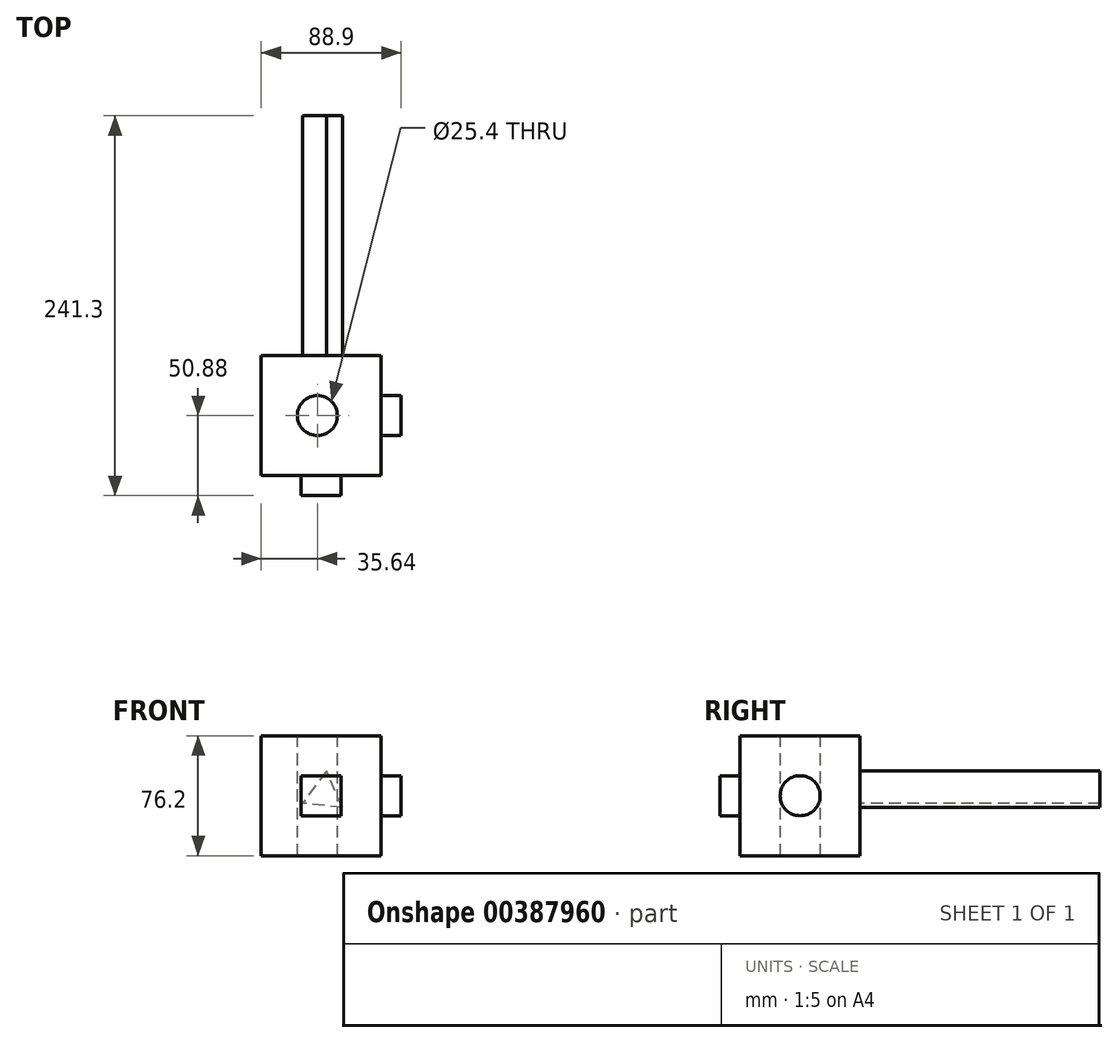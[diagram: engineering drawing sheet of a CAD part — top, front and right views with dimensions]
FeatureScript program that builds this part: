
annotation { "Feature Type Name" : "Feature", "Feature Type Description" : "" }
export const myFeature = defineFeature(function(context is Context, id is Id, definition is map)
    precondition{}
    {
        {
            var Q0;
            Q0=qCreatedBy(makeId("Front.planeOp"),FACE);
            var sketch = newSketch(context, id + "F0", { "sketchPlane" : qUnion([Q0])});
            skLineSegment(sketch, "E0.bottom", {"start": v(-35.64, -57.17) * mm, "end": v(40.56, -57.17) * mm});
            skLineSegment(sketch, "E0.top", {"start": v(-35.64, 19.03) * mm, "end": v(40.56, 19.03) * mm});
            skLineSegment(sketch, "E0.left", {"start": v(-35.64, -57.17) * mm, "end": v(-35.64, 19.03) * mm});
            skLineSegment(sketch, "E0.right", {"start": v(40.56, -57.17) * mm, "end": v(40.56, 19.03) * mm});
            skSolve(sketch);
        }
        {
            var Q0;
            Q0=makeQuery(id+"F0.imprint","IMPRINT",FACE,{"disambiguationData":[TD([[makeQuery(id+"F0.imprint","IMPRINT",EDGE,{"derivedFrom":sQuery(id+"F0.wireOp",EDGE,"E0.bottom")}),1.0]])]});
            extrude(context, id + "F1", {"entities" : qUnion([Q0]), "depth" : 76.2 * mm});
        }
        {
            var Q0;
            Q0=makeQuery(id+"F1.opExtrude","SWEPT_FACE",FACE,{"disambiguationData":[OSD([sQuery(id+"F0.wireOp",EDGE,"E0.top")])]});
            var sketch = newSketch(context, id + "F2", { "sketchPlane" : qUnion([Q0])});
            skPoint(sketch, "E1", {"position": v(0, -38.02) * mm});
            skSolve(sketch);
        }
        {
            var Q0;
            Q0=sQuery(id+"F2.wireOp",VERTEX,"E1");
            var Q1;
            Q1=makeQuery(id+"F1.opExtrude","SWEPT_BODY",BODY,{"disambiguationData":[OSD([sQuery(id+"F0.wireOp",EDGE,"E0.bottom"),sQuery(id+"F0.wireOp",EDGE,"E0.top"),sQuery(id+"F0.wireOp",EDGE,"E0.left"),sQuery(id+"F0.wireOp",EDGE,"E0.right")])]});
            hole(context, id + "F3", {"style" : HoleStyle.SIMPLE, "endStyle" : HoleEndStyle.THROUGH, "holeDiameter" : 25.4 * mm, "isTappedThrough" : true, "tappedDepth" : 12.7 * mm, "tapClearance" : 3, "locations" : qUnion([Q0]), "scope" : qUnion([Q1])});
        }
        {
            var Q0;
            Q0=makeQuery(id+"F1.opExtrude","CAP_FACE",FACE,{"disambiguationData":[OSD([sQuery(id+"F0.wireOp",EDGE,"E0.bottom"),sQuery(id+"F0.wireOp",EDGE,"E0.top"),sQuery(id+"F0.wireOp",EDGE,"E0.left"),sQuery(id+"F0.wireOp",EDGE,"E0.right")])],"isStart":false});
            var sketch = newSketch(context, id + "F4", { "sketchPlane" : qUnion([Q0])});
            skLineSegment(sketch, "E2.bottom", {"start": v(-10.24, -31.77) * mm, "end": v(15.16, -31.77) * mm});
            skLineSegment(sketch, "E2.top", {"start": v(-10.24, -6.37) * mm, "end": v(15.16, -6.37) * mm});
            skLineSegment(sketch, "E2.left", {"start": v(-10.24, -31.77) * mm, "end": v(-10.24, -6.37) * mm});
            skLineSegment(sketch, "E2.right", {"start": v(15.16, -31.77) * mm, "end": v(15.16, -6.37) * mm});
            skSolve(sketch);
        }
        {
            var Q0;
            Q0=makeQuery(id+"F4.imprint","IMPRINT",FACE,{"disambiguationData":[TD([[makeQuery(id+"F4.imprint","IMPRINT",EDGE,{"derivedFrom":sQuery(id+"F4.wireOp",EDGE,"E2.bottom")}),1.0]])]});
            extrude(context, id + "F5", {"entities" : qUnion([Q0]), "operationType" : NewBodyOperationType.ADD, "depth" : 12.7 * mm});
        }
        {
            var Q0;
            Q0=makeQuery(id+"F1.opExtrude","SWEPT_FACE",FACE,{"disambiguationData":[OSD([sQuery(id+"F0.wireOp",EDGE,"E0.right")])]});
            var sketch = newSketch(context, id + "F6", { "sketchPlane" : qUnion([Q0])});
            skCircle(sketch, "E3", {"center": v(-38.1, -19.07) * mm, "radius": 12.7 * mm});
            skSolve(sketch);
        }
        {
            var Q0;
            Q0 = qSketchRegion(id + "F6", true);
            extrude(context, id + "F7", {"entities" : qUnion([Q0]), "operationType" : NewBodyOperationType.ADD, "depth" : 12.7 * mm});
        }
        {
            var Q0;
            Q0=makeQuery(id+"F1.opExtrude","CAP_FACE",FACE,{"disambiguationData":[OSD([sQuery(id+"F0.wireOp",EDGE,"E0.bottom"),sQuery(id+"F0.wireOp",EDGE,"E0.top"),sQuery(id+"F0.wireOp",EDGE,"E0.left"),sQuery(id+"F0.wireOp",EDGE,"E0.right")])],"isStart":true});
            var sketch = newSketch(context, id + "F8", { "sketchPlane" : qUnion([Q0])});
            skLineSegment(sketch, "E4", {"start": v(-15.93, -26.63) * mm, "end": v(-5.77, -3.35) * mm});
            skLineSegment(sketch, "E5", {"start": v(-5.77, -3.35) * mm, "end": v(9.3, -23.78) * mm});
            skLineSegment(sketch, "E6", {"start": v(-15.93, -26.63) * mm, "end": v(9.3, -23.78) * mm});
            skPoint(sketch, "E7", {"position": v(-4.58, -6.37) * mm});
            skSolve(sketch);
        }
        {
            var Q0;
            Q0=makeQuery(id+"F8.imprint","IMPRINT",FACE,{"disambiguationData":[TD([[makeQuery(id+"F8.imprint","IMPRINT",EDGE,{"derivedFrom":sQuery(id+"F8.wireOp",EDGE,"E4")}),-1.0]])]});
            extrude(context, id + "F9", {"entities" : qUnion([Q0]), "operationType" : NewBodyOperationType.ADD, "depth" : 152.4 * mm});
        }
    });
